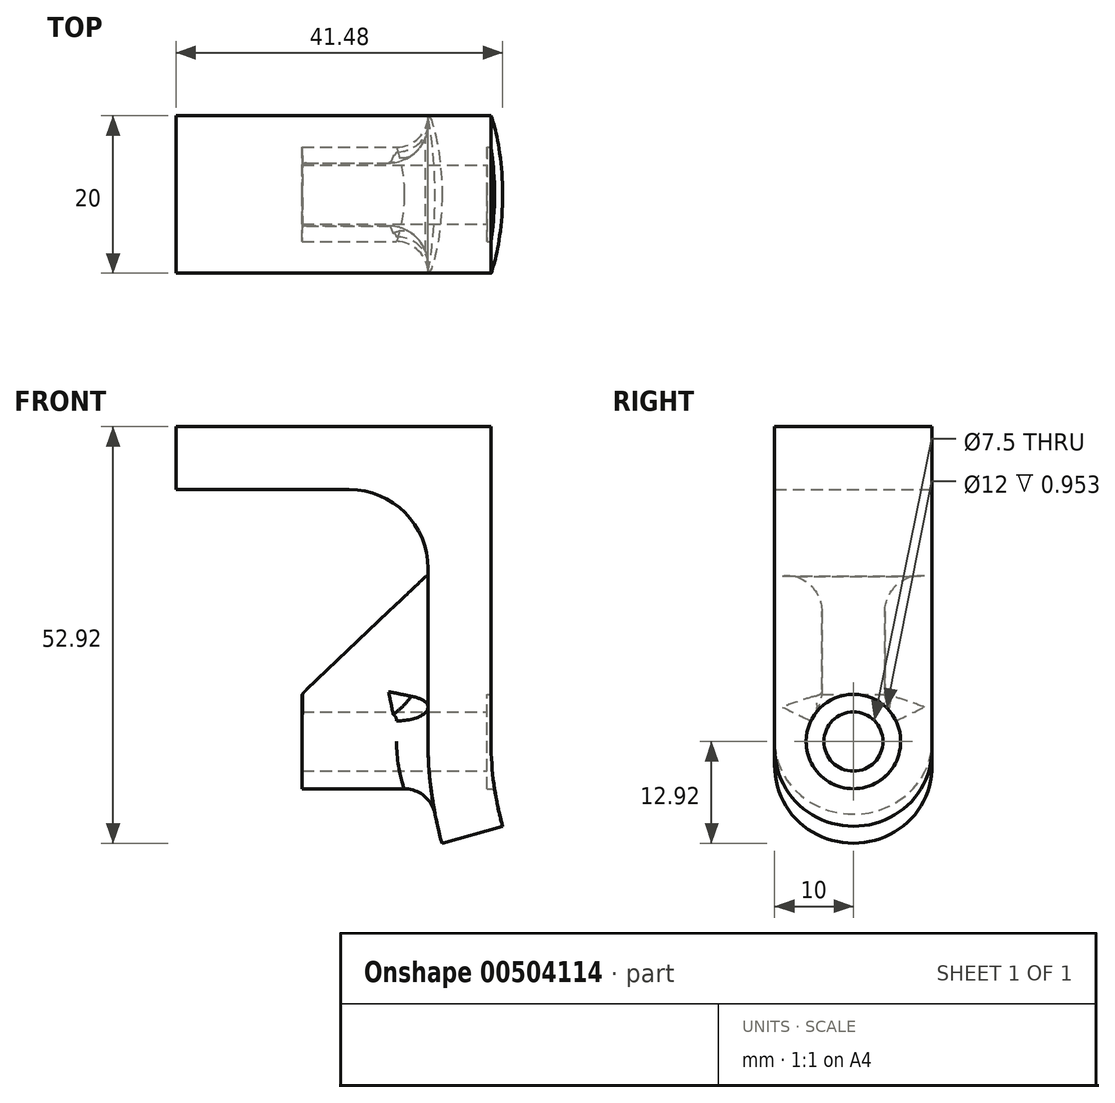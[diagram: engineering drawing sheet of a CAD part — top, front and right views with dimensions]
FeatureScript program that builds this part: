
annotation { "Feature Type Name" : "Feature", "Feature Type Description" : "" }
export const myFeature = defineFeature(function(context is Context, id is Id, definition is map)
    precondition{}
    {
        {
            var Q0;
            Q0=qCreatedBy(makeId("Front.planeOp"),FACE);
            var sketch = newSketch(context, id + "F0", { "sketchPlane" : qUnion([Q0])});
            skArc(sketch, "E0", {"start": v(-40, 0) * mm, "mid": v(-39.63, -5.43) * mm, "end": v(-38.52, -10.77) * mm});
            skPoint(sketch, "E1", {"position": v(-40, 0) * mm});
            skLineSegment(sketch, "E2", {"start": v(-40, 0) * mm, "end": v(-40, 40) * mm, "construction": true});
            skPoint(sketch, "E3", {"position": v(0, 40) * mm});
            skLineSegment(sketch, "E4", {"start": v(-40, 40) * mm, "end": v(-48, 40) * mm, "construction": true});
            skLineSegment(sketch, "E5", {"start": v(-48, 40) * mm, "end": v(-80, 40) * mm, "construction": true});
            skLineSegment(sketch, "E6", {"start": v(-58.66, 0) * mm, "end": v(-28.84, 0) * mm, "construction": true});
            skLineSegment(sketch, "E7", {"start": v(-48, 36.36) * mm, "end": v(-48, 0) * mm, "construction": true});
            skLineSegment(sketch, "E8", {"start": v(-80, 32) * mm, "end": v(-48, 32) * mm, "construction": true});
            skLineSegment(sketch, "E9", {"start": v(-80, 40) * mm, "end": v(-80, 32) * mm, "construction": true});
            skArc(sketch, "E10", {"start": v(-48, 0) * mm, "mid": v(-47.55, -6.52) * mm, "end": v(-46.23, -12.92) * mm});
            skPoint(sketch, "E11", {"position": v(-40, 40) * mm});
            skPoint(sketch, "E12", {"position": v(-59.61, 40) * mm});
            skLineSegment(sketch, "E13", {"start": v(-40, 40) * mm, "end": v(-80, 40) * mm});
            skLineSegment(sketch, "E14", {"start": v(-80, 32) * mm, "end": v(-80, 40) * mm});
            skLineSegment(sketch, "E15", {"start": v(-80, 32) * mm, "end": v(-48, 32) * mm});
            skLineSegment(sketch, "E16", {"start": v(-48, 32) * mm, "end": v(-48, 0) * mm});
            skLineSegment(sketch, "E17", {"start": v(-40, 40) * mm, "end": v(-40, 0) * mm});
            skPoint(sketch, "E18.endSnap0", {"position": v(-45.66, -14.8) * mm});
            skPoint(sketch, "E19", {"position": v(-46.23, -12.92) * mm});
            skPoint(sketch, "E20", {"position": v(-38.52, -10.77) * mm});
            skPoint(sketch, "E18.end.orphan", {"position": v(-52.96, -14.8) * mm});
            skLineSegment(sketch, "E21", {"start": v(-46.23, -12.92) * mm, "end": v(-38.52, -10.77) * mm});
            skSolve(sketch);
        }
        {
            var Q0;
            Q0 = qSketchRegion(id + "F0", true);
            var Q1;
            Q1=makeQuery(id+"F0.imprint","IMPRINT",FACE,{"disambiguationData":[TD([[makeQuery(id+"F0.imprint","IMPRINT",EDGE,{"derivedFrom":sQuery(id+"F0.wireOp",EDGE,"E0")}),-1.0]])]});
            extrude(context, id + "F1", {"entities" : qUnion([Q0, Q1]), "endBound" : BoundingType.SYMMETRIC, "depth" : 20 * mm});
        }
        {
            var Q0;
            Q0=qCreatedBy(makeId("Right.planeOp"),FACE);
            var sketch = newSketch(context, id + "F2", { "sketchPlane" : qUnion([Q0])});
            skCircle(sketch, "E22", {"center": v(0, 0) * mm, "radius": 3.75 * mm});
            skCircle(sketch, "E23", {"center": v(0, 0) * mm, "radius": 6 * mm});
            skSolve(sketch);
        }
        {
            var Q0;
            Q0=makeQuery(id+"F2.imprint","IMPRINT",FACE,{"disambiguationData":[TD([[makeQuery(id+"F2.imprint","IMPRINT",EDGE,{"derivedFrom":sQuery(id+"F2.wireOp",EDGE,"E22")}),1.0]])]});
            var Q1;
            Q1=sQuery(id+"F2.wireOp",EDGE,"E22");
            extrude(context, id + "F3", {"entities" : qUnion([Q0]), "operationType" : NewBodyOperationType.REMOVE, "surfaceEntities" : qUnion([Q1]), "oppositeDirection" : true, "depth" : 64.2 * mm});
        }
        {
            var Q0;
            Q0 = qSketchRegion(id + "F2", true);
            extrude(context, id + "F4", {"entities" : qUnion([Q0]), "operationType" : NewBodyOperationType.ADD, "oppositeDirection" : true, "depth" : 52 * mm});
        }
        {
            var Q0;
            Q0=makeQuery(id+"F4.opExtrude","CAP_FACE",FACE,{"disambiguationData":[OSD([sQuery(id+"F2.wireOp",EDGE,"E22"),sQuery(id+"F2.wireOp",EDGE,"E23")])],"isStart":true});
            extrude(context, id + "F5", {"entities" : qUnion([Q0]), "operationType" : NewBodyOperationType.REMOVE, "oppositeDirection" : true, "depth" : 40.5 * mm});
        }
        {
            var Q0;
            Q0=makeQuery(id+"F1.opExtrude","SWEPT_EDGE",EDGE,{"disambiguationData":[OSD([sQuery(id+"F0.wireOp",EDGE,"E15"),sQuery(id+"F0.wireOp",EDGE,"E16")])]});
            var Q1;
            Q1=makeQuery(id+"F1.opExtrude","CAP_EDGE",EDGE,{"disambiguationData":[OSD([sQuery(id+"F0.wireOp",EDGE,"E21")])],"isStart":true});
            var Q2;
            Q2=makeQuery(id+"F1.opExtrude","CAP_EDGE",EDGE,{"disambiguationData":[OSD([sQuery(id+"F0.wireOp",EDGE,"E21")])],"isStart":false});
            fillet(context, id + "F6", {"entities" : qUnion([Q0, Q1, Q2]), "radius" : 10 * mm, "tangentPropagation" : true, "allowEdgeOverflow" : false});
        }
        {
            var Q0;
            Q0=makeQuery(id+"F4.boolean.opBoolean","INTERSECT",EDGE,{"derivedFrom":[makeQuery(id+"F1.opExtrude","SWEPT_FACE",FACE,{"disambiguationData":[OSD([sQuery(id+"F0.wireOp",EDGE,"E10")])]}),makeQuery(id+"F4.opExtrude","SWEPT_FACE",FACE,{"disambiguationData":[OSD([sQuery(id+"F2.wireOp",EDGE,"E23")])]})]});
            fillet(context, id + "F7", {"entities" : qUnion([Q0]), "radius" : 4 * mm, "tangentPropagation" : true, "allowEdgeOverflow" : false});
        }
        {
            var Q0;
            Q0=makeQuery(id+"F4.opExtrude","CAP_FACE",FACE,{"disambiguationData":[OSD([sQuery(id+"F2.wireOp",EDGE,"E22"),sQuery(id+"F2.wireOp",EDGE,"E23")])],"isStart":false});
            extrude(context, id + "F8", {"entities" : qUnion([Q0]), "operationType" : NewBodyOperationType.ADD, "depth" : 12 * mm});
        }
        {
            var Q0;
            Q0=qCreatedBy(makeId("Front.planeOp"),FACE);
            var sketch = newSketch(context, id + "F9", { "sketchPlane" : qUnion([Q0])});
            skLineSegment(sketch, "E24", {"start": v(-64, 6.04) * mm, "end": v(-48.28, 20.98) * mm});
            skLineSegment(sketch, "E25", {"start": v(-64, 6.04) * mm, "end": v(-63.96, 5.99) * mm});
            skLineSegment(sketch, "E26", {"start": v(-63.96, 5.99) * mm, "end": v(-44.3, 5.99) * mm});
            skLineSegment(sketch, "E27", {"start": v(-44.3, 5.99) * mm, "end": v(-44.3, 21.4) * mm});
            skLineSegment(sketch, "E28", {"start": v(-44.3, 21.4) * mm, "end": v(-48.28, 20.98) * mm});
            skSolve(sketch);
        }
        {
            var Q0;
            Q0 = qSketchRegion(id + "F9", true);
            var Q1;
            Q1=makeQuery(id+"F9.imprint","IMPRINT",FACE,{"disambiguationData":[TD([[makeQuery(id+"F9.imprint","IMPRINT",EDGE,{"derivedFrom":sQuery(id+"F9.wireOp",EDGE,"E24")}),-1.0]])]});
            extrude(context, id + "F10", {"entities" : qUnion([Q0, Q1]), "operationType" : NewBodyOperationType.ADD, "endBound" : BoundingType.SYMMETRIC, "depth" : 8 * mm});
        }
        {
            var Q0;
            {var subQ0=sQuery(id+"F9.wireOp",EDGE,"E26");var subQ1=sQuery(id+"F9.wireOp",EDGE,"E25");Q0=makeQuery(id+"F10.boolean.opBoolean","SPLIT",FACE,{"disambiguationData":[TD([makeQuery(id+"F10.opExtrude","CAP_FACE",FACE,{"disambiguationData":[OSD([sQuery(id+"F9.wireOp",EDGE,"E24"),subQ1,subQ0,sQuery(id+"F9.wireOp",EDGE,"E27"),sQuery(id+"F9.wireOp",EDGE,"E28")])],"isStart":true})])],"derivedFrom":makeQuery(id+"F10.opExtrude","SWEPT_FACE",FACE,{"disambiguationData":[OSD([subQ0])]})});}
            var Q1;
            {var subQ2=sQuery(id+"F9.wireOp",EDGE,"E26");var subQ3=sQuery(id+"F9.wireOp",EDGE,"E25");Q1=makeQuery(id+"F10.boolean.opBoolean","SPLIT",FACE,{"disambiguationData":[TD([makeQuery(id+"F10.opExtrude","CAP_FACE",FACE,{"disambiguationData":[OSD([sQuery(id+"F9.wireOp",EDGE,"E24"),subQ3,subQ2,sQuery(id+"F9.wireOp",EDGE,"E27"),sQuery(id+"F9.wireOp",EDGE,"E28")])],"isStart":false})])],"derivedFrom":makeQuery(id+"F10.opExtrude","SWEPT_FACE",FACE,{"disambiguationData":[OSD([subQ2])]})});}
            extrude(context, id + "F11", {"entities" : qUnion([Q0, Q1]), "operationType" : NewBodyOperationType.ADD, "depth" : 5 * mm});
        }
        {
            var Q0;
            {var subQ0=sQuery(id+"F9.wireOp",EDGE,"E26");var subQ1=sQuery(id+"F2.wireOp",EDGE,"E23");var subQ2=sQuery(id+"F2.wireOp",EDGE,"E22");var subQ3=sQuery(id+"F0.wireOp",EDGE,"E16");Q0=makeQuery(id+"F11.boolean.opBoolean","INTERSECT",EDGE,{"derivedFrom":[makeQuery(id+"F8.boolean.opBoolean","MERGE",FACE,{"derivedFrom":[makeQuery(id+"F4.boolean.opBoolean","SPLIT",FACE,{"disambiguationData":[TD([makeQuery(id+"F1.opExtrude","SWEPT_FACE",FACE,{"disambiguationData":[OSD([sQuery(id+"F0.wireOp",EDGE,"E10")])]})])],"derivedFrom":makeQuery(id+"F4.opExtrude","SWEPT_FACE",FACE,{"disambiguationData":[OSD([subQ1])]})}),makeQuery(id+"F8.opExtrude","SWEPT_FACE",FACE,{"disambiguationData":[OSD([subQ3,subQ2,subQ1])]})]}),makeQuery(id+"F11.opExtrude","SWEPT_FACE",FACE,{"disambiguationData":[OSD([subQ0]),TDD([makeQuery(id+"F10.opExtrude","CAP_EDGE",EDGE,{"disambiguationData":[OSD([subQ0])],"isStart":true})])]})]});}
            var Q1;
            {var subQ0=sQuery(id+"F9.wireOp",EDGE,"E26");var subQ1=sQuery(id+"F2.wireOp",EDGE,"E23");var subQ2=sQuery(id+"F2.wireOp",EDGE,"E22");var subQ3=sQuery(id+"F0.wireOp",EDGE,"E16");Q1=makeQuery(id+"F11.boolean.opBoolean","INTERSECT",EDGE,{"derivedFrom":[makeQuery(id+"F8.boolean.opBoolean","MERGE",FACE,{"derivedFrom":[makeQuery(id+"F4.boolean.opBoolean","SPLIT",FACE,{"disambiguationData":[TD([makeQuery(id+"F1.opExtrude","SWEPT_FACE",FACE,{"disambiguationData":[OSD([sQuery(id+"F0.wireOp",EDGE,"E10")])]})])],"derivedFrom":makeQuery(id+"F4.opExtrude","SWEPT_FACE",FACE,{"disambiguationData":[OSD([subQ1])]})}),makeQuery(id+"F8.opExtrude","SWEPT_FACE",FACE,{"disambiguationData":[OSD([subQ3,subQ2,subQ1])]})]}),makeQuery(id+"F11.opExtrude","SWEPT_FACE",FACE,{"disambiguationData":[OSD([subQ0]),TDD([makeQuery(id+"F10.opExtrude","CAP_EDGE",EDGE,{"disambiguationData":[OSD([subQ0])],"isStart":false})])]})]});}
            fillet(context, id + "F12", {"entities" : qUnion([Q0, Q1]), "radius" : 5 * mm, "tangentPropagation" : true, "allowEdgeOverflow" : false});
        }
        {
            var Q0;
            Q0=makeQuery(id+"F10.opExtrude","SWEPT_EDGE",EDGE,{"disambiguationData":[OSD([sQuery(id+"F9.wireOp",EDGE,"E24"),sQuery(id+"F9.wireOp",EDGE,"E25")])]});
            fillet(context, id + "F13", {"entities" : qUnion([Q0]), "radius" : 5 * mm, "tangentPropagation" : true, "allowEdgeOverflow" : false});
        }
        {
            var Q0;
            {var subQ0=sQuery(id+"F9.wireOp",EDGE,"E26");var subQ3=sQuery(id+"F2.wireOp",EDGE,"E22");var subQ7=sQuery(id+"F9.wireOp",EDGE,"E25");var subQ8=makeQuery(id+"F10.opExtrude","CAP_FACE",FACE,{"disambiguationData":[OSD([sQuery(id+"F9.wireOp",EDGE,"E24"),subQ7,subQ0,sQuery(id+"F9.wireOp",EDGE,"E27"),sQuery(id+"F9.wireOp",EDGE,"E28")])],"isStart":false});Q0=makeQuery(id+"F11.boolean.opBoolean","SPLIT",FACE,{"disambiguationData":[TD([makeQuery(id+"F3.boolean.opBoolean","COPY",FACE,{"derivedFrom":makeQuery(id+"F3.opExtrude","SWEPT_FACE",FACE,{"disambiguationData":[OSD([subQ3])]})})])],"derivedFrom":makeQuery(id+"F11.opExtrude","SWEPT_FACE",FACE,{"disambiguationData":[OSD([subQ7,subQ0]),TDD([makeQuery(id+"F10.boolean.opBoolean","SPLIT",EDGE,{"disambiguationData":[TD([subQ8])],"derivedFrom":makeQuery(id+"F10.opExtrude","SWEPT_EDGE",EDGE,{"disambiguationData":[OSD([subQ7,subQ0])]})})])]})});}
            var Q1;
            {var subQ0=sQuery(id+"F9.wireOp",EDGE,"E26");var subQ3=sQuery(id+"F2.wireOp",EDGE,"E22");var subQ7=sQuery(id+"F9.wireOp",EDGE,"E25");var subQ8=makeQuery(id+"F10.opExtrude","CAP_FACE",FACE,{"disambiguationData":[OSD([sQuery(id+"F9.wireOp",EDGE,"E24"),subQ7,subQ0,sQuery(id+"F9.wireOp",EDGE,"E27"),sQuery(id+"F9.wireOp",EDGE,"E28")])],"isStart":true});Q1=makeQuery(id+"F11.boolean.opBoolean","SPLIT",FACE,{"disambiguationData":[TD([makeQuery(id+"F3.boolean.opBoolean","COPY",FACE,{"derivedFrom":makeQuery(id+"F3.opExtrude","SWEPT_FACE",FACE,{"disambiguationData":[OSD([subQ3])]})})])],"derivedFrom":makeQuery(id+"F11.opExtrude","SWEPT_FACE",FACE,{"disambiguationData":[OSD([subQ7,subQ0]),TDD([makeQuery(id+"F10.boolean.opBoolean","SPLIT",EDGE,{"disambiguationData":[TD([subQ8])],"derivedFrom":makeQuery(id+"F10.opExtrude","SWEPT_EDGE",EDGE,{"disambiguationData":[OSD([subQ7,subQ0])]})})])]})});}
            extrude(context, id + "F14", {"entities" : qUnion([Q0, Q1]), "operationType" : NewBodyOperationType.REMOVE, "oppositeDirection" : true, "depth" : 26 * mm});
        }
    });
